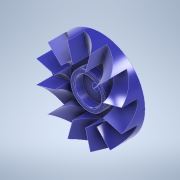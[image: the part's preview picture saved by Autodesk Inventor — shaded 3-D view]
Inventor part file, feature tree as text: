
AUTODESK INVENTOR PART (.ipt)
format: ipt  version: 2021 (Build 250183000, 183)  size: 320,000 bytes
history: native  units: in
note: dims shown in document units (in); Inventor stores cm internally (conversion verified against a paired STEP export)
features: sketch x7, extrude x5, split x2, other x2, plane x1, loft x1, pattern_circular x1, fillet x1
ambient origin geometry x8: Origin, YZ Plane, XZ Plane, XY Plane, X Axis, Y Axis, Z Axis, Center Point
bodies: Solid1 (feature_tree)
feature tree (20):
  extrude  "Extrusion1"  Depth=1.0in TaperAngle=0.0deg
  extrude  "Extrusion2"  Depth=0.75in TaperAngle=0.0deg
  sketch  "Sketch3"  dims[d8=2.5in d10=0.515in]
  plane  "Work Plane1"
  split  "Split3"
  split  "Split4"
  loft  "Loft1"
  extrude  "Extrusion3"  Depth=2.265in
  pattern_circular  "Circular Pattern2"  Count=12 Angle=360.0deg
  extrude  "Extrusion4"  Depth=0.35in
  fillet  "Fillet1"  Radius=0.35in
  extrude  "Extrusion5"  Depth=0.0312in
  sketch  "Sketch1"  dims[d0=4.0in d1=1.0in d2=0.0in]
  sketch  "Sketch2"  dims[d3=2.25in d4=0.75in d5=0.0in]
  sketch  "Sketch4"  dims[d11=0.0in d12=90.0deg d13=0.0in d14=90.0deg d18=2.265in]
  other  "Edges1"
  other  "Edges2"
  sketch  "Sketch6"  dims[d19=0.75in d20=0.0in d21=4.7244in d22=360.0deg]
  sketch  "Sketch7"  dims[d24=1.6in d25=1.2in d26=0.35in d27=0.0in]
  sketch  "Sketch8"  dims[d28=0.0312in d29=0.315in d30=0.0in d31=0.0in]
